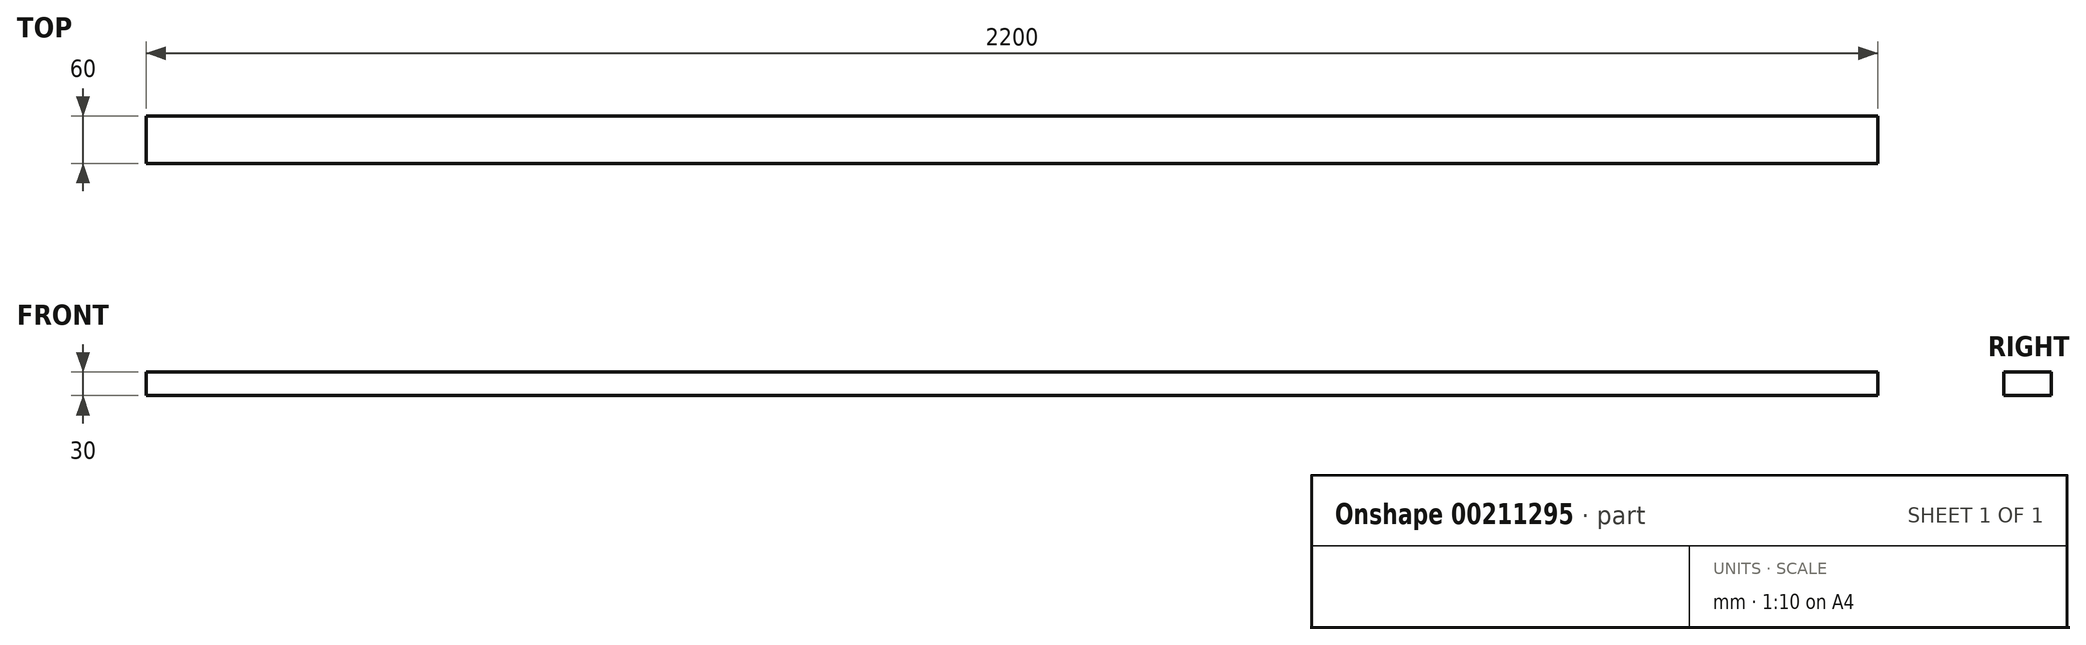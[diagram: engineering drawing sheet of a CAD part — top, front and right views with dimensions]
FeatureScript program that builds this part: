
annotation { "Feature Type Name" : "Feature", "Feature Type Description" : "" }
export const myFeature = defineFeature(function(context is Context, id is Id, definition is map)
    precondition{}
    {
        {
            var Q0;
            Q0=qCreatedBy(makeId("Top.planeOp"),FACE);
            var sketch = newSketch(context, id + "F0", { "sketchPlane" : qUnion([Q0])});
            skLineSegment(sketch, "E0.bottom", {"start": v(1100, -30) * mm, "end": v(-1100, -30) * mm});
            skLineSegment(sketch, "E0.top", {"start": v(1100, 30) * mm, "end": v(-1100, 30) * mm});
            skLineSegment(sketch, "E0.left", {"start": v(1100, -30) * mm, "end": v(1100, 30) * mm});
            skLineSegment(sketch, "E0.right", {"start": v(-1100, -30) * mm, "end": v(-1100, 30) * mm});
            skPoint(sketch, "E0.middle", {"position": v(0, 0) * mm});
            skSolve(sketch);
        }
        {
            var Q0;
            Q0=makeQuery(id+"F0.imprint","IMPRINT",FACE,{"disambiguationData":[TD([[makeQuery(id+"F0.imprint","IMPRINT",EDGE,{"derivedFrom":sQuery(id+"F0.wireOp",EDGE,"E0.bottom")}),-1.0]])]});
            extrude(context, id + "F1", {"entities" : qUnion([Q0]), "depth" : 30 * mm});
        }
    });
